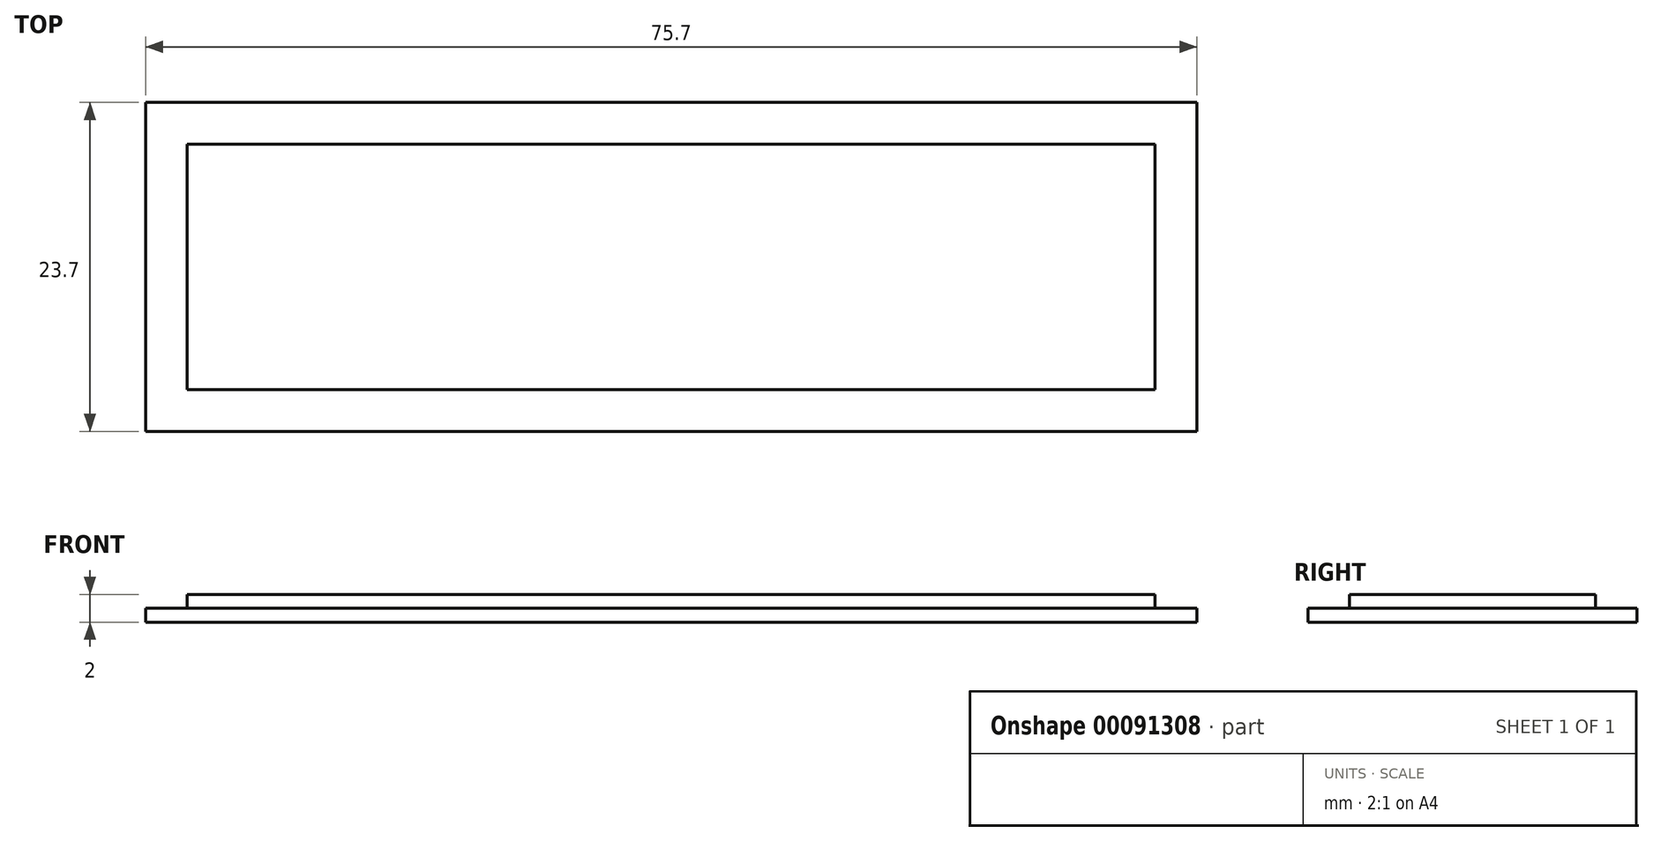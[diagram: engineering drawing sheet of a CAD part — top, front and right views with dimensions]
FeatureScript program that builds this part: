
annotation { "Feature Type Name" : "Feature", "Feature Type Description" : "" }
export const myFeature = defineFeature(function(context is Context, id is Id, definition is map)
    precondition{}
    {
        {
            var Q0;
            Q0=qCreatedBy(makeId("Top.planeOp"),FACE);
            var sketch = newSketch(context, id + "F0", { "sketchPlane" : qUnion([Q0])});
            skLineSegment(sketch, "E0.bottom", {"start": v(34.85, -8.85) * mm, "end": v(-34.85, -8.85) * mm});
            skLineSegment(sketch, "E0.top", {"start": v(34.85, 8.85) * mm, "end": v(-34.85, 8.85) * mm});
            skLineSegment(sketch, "E0.left", {"start": v(34.85, -8.85) * mm, "end": v(34.85, 8.85) * mm});
            skLineSegment(sketch, "E0.right", {"start": v(-34.85, -8.85) * mm, "end": v(-34.85, 8.85) * mm});
            skPoint(sketch, "E0.middle", {"position": v(0, 0) * mm});
            skSolve(sketch);
        }
        {
            var Q0;
            Q0 = qSketchRegion(id + "F0", true);
            extrude(context, id + "F1", {"entities" : qUnion([Q0]), "depth" : 1 * mm});
        }
        {
            var Q0;
            Q0=makeQuery(id+"F1.opExtrude","CAP_FACE",FACE,{"disambiguationData":[OSD([sQuery(id+"F0.wireOp",EDGE,"E0.bottom"),sQuery(id+"F0.wireOp",EDGE,"E0.top"),sQuery(id+"F0.wireOp",EDGE,"E0.left"),sQuery(id+"F0.wireOp",EDGE,"E0.right")])],"isStart":false});
            var sketch = newSketch(context, id + "F2", { "sketchPlane" : qUnion([Q0])});
            skLineSegment(sketch, "E1.0.0", {"start": v(-34.85, -8.85) * mm, "end": v(34.85, -8.85) * mm});
            skLineSegment(sketch, "E1.0.1", {"start": v(34.85, -8.85) * mm, "end": v(34.85, 8.85) * mm});
            skLineSegment(sketch, "E1.0.2", {"start": v(34.85, 8.85) * mm, "end": v(-34.85, 8.85) * mm});
            skLineSegment(sketch, "E1.0.3", {"start": v(-34.85, 8.85) * mm, "end": v(-34.85, -8.85) * mm});
            skLineSegment(sketch, "E2.0", {"start": v(-34.45, 8.45) * mm, "end": v(-34.45, -8.45) * mm});
            skLineSegment(sketch, "E2.1", {"start": v(34.45, 8.45) * mm, "end": v(-34.45, 8.45) * mm});
            skLineSegment(sketch, "E2.2", {"start": v(34.45, -8.45) * mm, "end": v(34.45, 8.45) * mm});
            skLineSegment(sketch, "E2.3", {"start": v(-34.45, -8.45) * mm, "end": v(34.45, -8.45) * mm});
            skLineSegment(sketch, "E3.0", {"start": v(-29.85, -3.85) * mm, "end": v(29.85, -3.85) * mm});
            skLineSegment(sketch, "E3.1", {"start": v(-29.85, 3.85) * mm, "end": v(-29.85, -3.85) * mm});
            skLineSegment(sketch, "E3.2", {"start": v(29.85, 3.85) * mm, "end": v(-29.85, 3.85) * mm});
            skLineSegment(sketch, "E3.3", {"start": v(29.85, -3.85) * mm, "end": v(29.85, 3.85) * mm});
            skSolve(sketch);
        }
        {
            var Q0;
            Q0=makeQuery(id+"F1.opExtrude","CAP_FACE",FACE,{"disambiguationData":[OSD([sQuery(id+"F0.wireOp",EDGE,"E0.bottom"),sQuery(id+"F0.wireOp",EDGE,"E0.top"),sQuery(id+"F0.wireOp",EDGE,"E0.left"),sQuery(id+"F0.wireOp",EDGE,"E0.right")])],"isStart":true});
            var sketch = newSketch(context, id + "F3", { "sketchPlane" : qUnion([Q0])});
            skLineSegment(sketch, "E4.0", {"start": v(-34.85, -8.85) * mm, "end": v(-34.85, 8.85) * mm});
            skLineSegment(sketch, "E5.0", {"start": v(-34.85, 8.85) * mm, "end": v(34.85, 8.85) * mm});
            skLineSegment(sketch, "E6.0", {"start": v(34.85, -8.85) * mm, "end": v(-34.85, -8.85) * mm});
            skLineSegment(sketch, "E7.0", {"start": v(34.85, 8.85) * mm, "end": v(34.85, -8.85) * mm});
            skLineSegment(sketch, "E8.0", {"start": v(-37.85, 11.85) * mm, "end": v(37.85, 11.85) * mm});
            skLineSegment(sketch, "E8.1", {"start": v(-37.85, -11.85) * mm, "end": v(-37.85, 11.85) * mm});
            skLineSegment(sketch, "E8.2", {"start": v(37.85, -11.85) * mm, "end": v(-37.85, -11.85) * mm});
            skLineSegment(sketch, "E8.3", {"start": v(37.85, 11.85) * mm, "end": v(37.85, -11.85) * mm});
            skSolve(sketch);
        }
        {
            var Q0;
            Q0=makeQuery(id+"F3.imprint","IMPRINT",FACE,{"disambiguationData":[TD([[makeQuery(id+"F3.imprint","IMPRINT",EDGE,{"derivedFrom":sQuery(id+"F3.wireOp",EDGE,"E4.0")}),-1.0]])]});
            var Q1;
            Q1=makeQuery(id+"F3.imprint","IMPRINT",FACE,{"disambiguationData":[TD([[makeQuery(id+"F3.imprint","IMPRINT",EDGE,{"derivedFrom":sQuery(id+"F3.wireOp",EDGE,"E4.0")}),1.0]])]});
            extrude(context, id + "F4", {"entities" : qUnion([Q0, Q1]), "operationType" : NewBodyOperationType.ADD, "depth" : 1 * mm});
        }
    });
